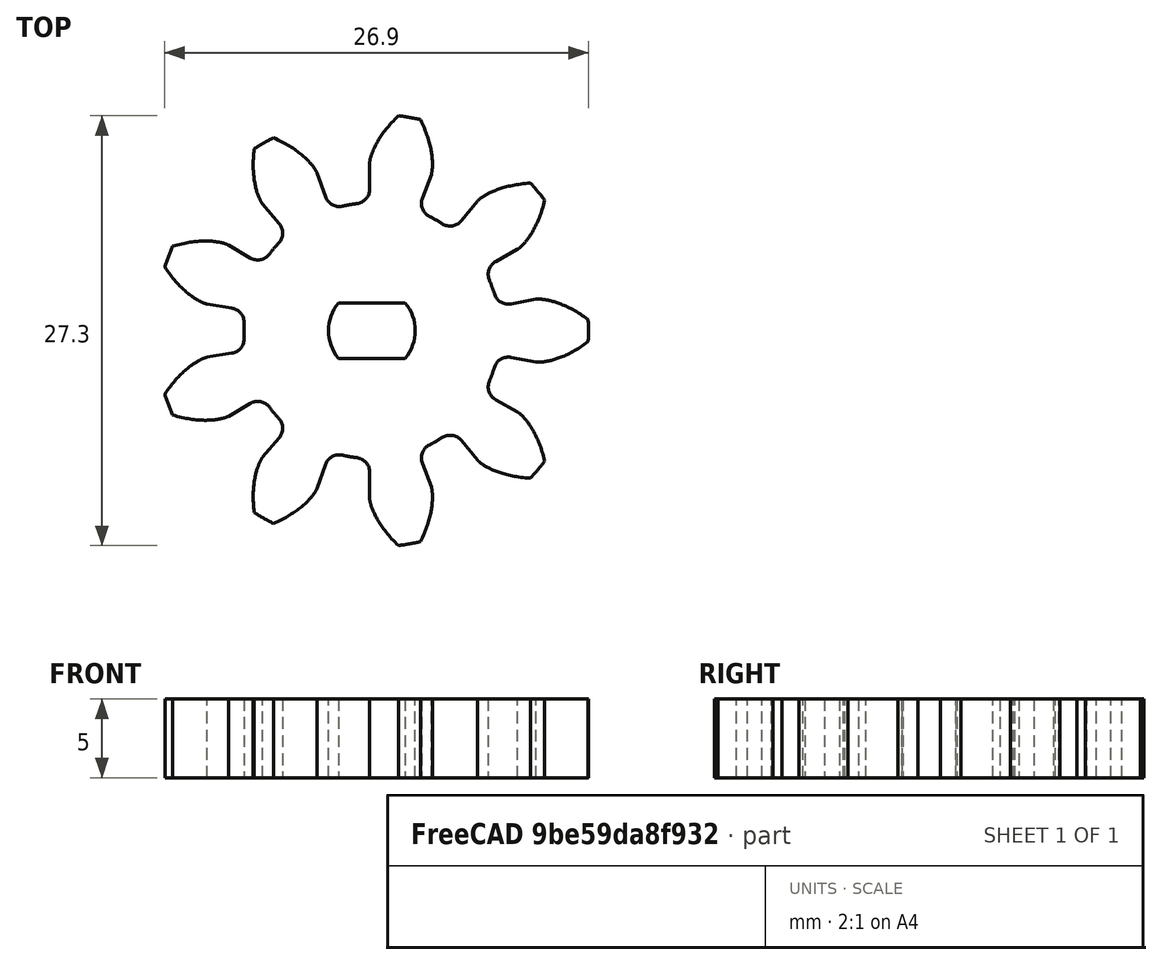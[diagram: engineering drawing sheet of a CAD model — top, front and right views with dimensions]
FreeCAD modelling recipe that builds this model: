
FCSTD DOCUMENT  (FreeCAD 0.16R6704 (Git))
Label: barn_door_tracker_9_teeth_gear
License: All rights reserved
LicenseURL: http://en.wikipedia.org/wiki/All_rights_reserved
objects: Part::Part2DObjectPython×1, PartDesign::Pad×1, Sketcher::SketchObject×1, PartDesign::Pocket×1
note: 6 computed .brp shape members not serialized (recipe doc carries the construction recipe); baked Part::Feature solids carry a one-line shape summary decoded from their .brp

FEATURE [Part::Part2DObjectPython] InvoluteGear  # Draft 2D object (typed FeaturePython)
  ExternalGear = true
  HighPrecision = true
  Modules = 2.5
  NumberOfTeeth = 9
  PressureAngle = 20
FEATURE [PartDesign::Pad] Pad
  Length = 5
  Length2 = 100
  Sketch = -> InvoluteGear
  Type = 0
FEATURE [Sketcher::SketchObject] Sketch
  Placement = pos=(0,0,5) rot=(0,0,1;0rad)
  Support = -> Pad [Face92]
  sketch-geometry (4):
    g0: ArcOfCircle CenterX=0 CenterY=0 CenterZ=0 NormalX=0 NormalY=0 NormalZ=1 Radius=2.75668 StartAngle=2.44642 EndAngle=3.83677
    g1: LineSegment StartX=-2.11696 StartY=1.76571 StartZ=0 EndX=2.11696 EndY=1.76571 EndZ=0
    g2: LineSegment StartX=2.11696 StartY=-1.76571 StartZ=0 EndX=-2.11696 EndY=-1.76571 EndZ=0
    g3: ArcOfCircle CenterX=0 CenterY=0 CenterZ=0 NormalX=0 NormalY=0 NormalZ=1 Radius=2.75668 StartAngle=5.58801 EndAngle=6.97836
  constraints (8):
    c: Coincident(g0,g-1)
    c: Horizontal(g1)
    c: Horizontal(g2)
    c: Coincident(g0,g1)
    c: Coincident(g3,g1)
    c: Equal(g0,g3)
    c: Coincident(g0,g2)
    c: Coincident(g0,g3)
FEATURE [PartDesign::Pocket] Pocket
  Length = 5
  Sketch = -> Sketch
  Type = 0
